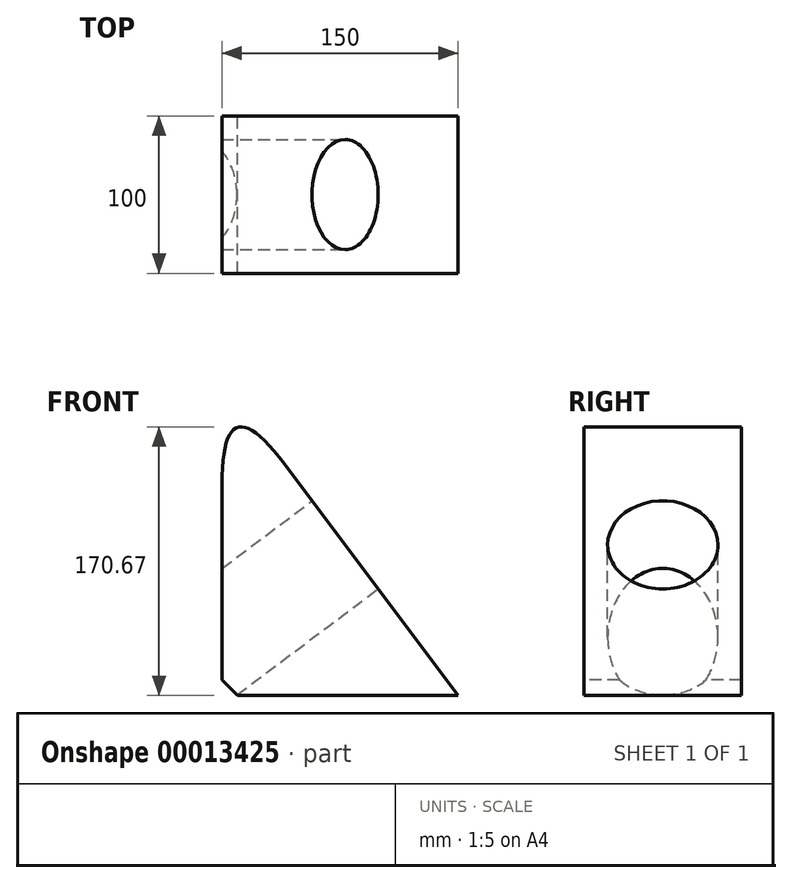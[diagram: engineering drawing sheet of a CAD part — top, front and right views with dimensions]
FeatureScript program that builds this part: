
annotation { "Feature Type Name" : "Feature", "Feature Type Description" : "" }
export const myFeature = defineFeature(function(context is Context, id is Id, definition is map)
    precondition{}
    {
        {
            var Q0;
            Q0=qCreatedBy(makeId("Front.planeOp"),FACE);
            var sketch = newSketch(context, id + "F0", { "sketchPlane" : qUnion([Q0])});
            skLineSegment(sketch, "E0", {"start": v(0, 0) * mm, "end": v(150, 0) * mm});
            skLineSegment(sketch, "E1", {"start": v(150, 0) * mm, "end": v(0, 200) * mm});
            skLineSegment(sketch, "E2", {"start": v(0, 200) * mm, "end": v(0, 0) * mm});
            skSolve(sketch);
        }
        {
            var Q0;
            Q0=makeQuery(id+"F0.imprint","IMPRINT",FACE,{"disambiguationData":[TD([[makeQuery(id+"F0.imprint","IMPRINT",EDGE,{"derivedFrom":sQuery(id+"F0.wireOp",EDGE,"E0")}),1.0]])]});
            extrude(context, id + "F1", {"entities" : qUnion([Q0]), "endBound" : BoundingType.SYMMETRIC, "depth" : 100 * mm});
        }
        {
            var Q0;
            Q0=makeQuery(id+"F1.opExtrude","SWEPT_EDGE",EDGE,{"disambiguationData":[OSD([sQuery(id+"F0.wireOp",EDGE,"E1"),sQuery(id+"F0.wireOp",EDGE,"E2")])]});
            fillet(context, id + "F2", {"entities" : qUnion([Q0]), "radius" : 22 * mm, "rho" : 0.5, "crossSection" : FilletCrossSection.CONIC, "allowEdgeOverflow" : false});
        }
        {
            var Q0;
            Q0=makeQuery(id+"F1.opExtrude","SWEPT_EDGE",EDGE,{"disambiguationData":[OSD([sQuery(id+"F0.wireOp",EDGE,"E0"),sQuery(id+"F0.wireOp",EDGE,"E2")])]});
            chamfer(context, id + "F3", {"entities" : qUnion([Q0]), "width" : 10 * mm, "tangentPropagation" : true});
        }
        {
            var Q0;
            Q0=makeQuery(id+"F1.opExtrude","SWEPT_FACE",FACE,{"disambiguationData":[OSD([sQuery(id+"F0.wireOp",EDGE,"E1")])]});
            var sketch = newSketch(context, id + "F4", { "sketchPlane" : qUnion([Q0])});
            skFitSpline(sketch, "E3.0", {"points": [v(50, 94) * mm, v(16.67, 94) * mm, v(-16.67, 94) * mm, v(-50, 94) * mm]});
            skLineSegment(sketch, "E4.0", {"start": v(-50, -90) * mm, "end": v(50, -90) * mm});
            skLineSegment(sketch, "E5", {"start": v(0, -90) * mm, "end": v(0, 94) * mm, "construction": true});
            skCircle(sketch, "E6", {"center": v(0, 29.65) * mm, "radius": 35 * mm});
            skSolve(sketch);
        }
        {
            var Q0;
            Q0=makeQuery(id+"F4.imprint","IMPRINT",FACE,{"disambiguationData":[TD([[makeQuery(id+"F4.imprint","IMPRINT",EDGE,{"derivedFrom":sQuery(id+"F4.wireOp",EDGE,"E6")}),1.0]])]});
            extrude(context, id + "F5", {"entities" : qUnion([Q0]), "operationType" : NewBodyOperationType.REMOVE, "endBound" : BoundingType.UP_TO_NEXT, "oppositeDirection" : true, "depth" : 100 * mm});
        }
    });
